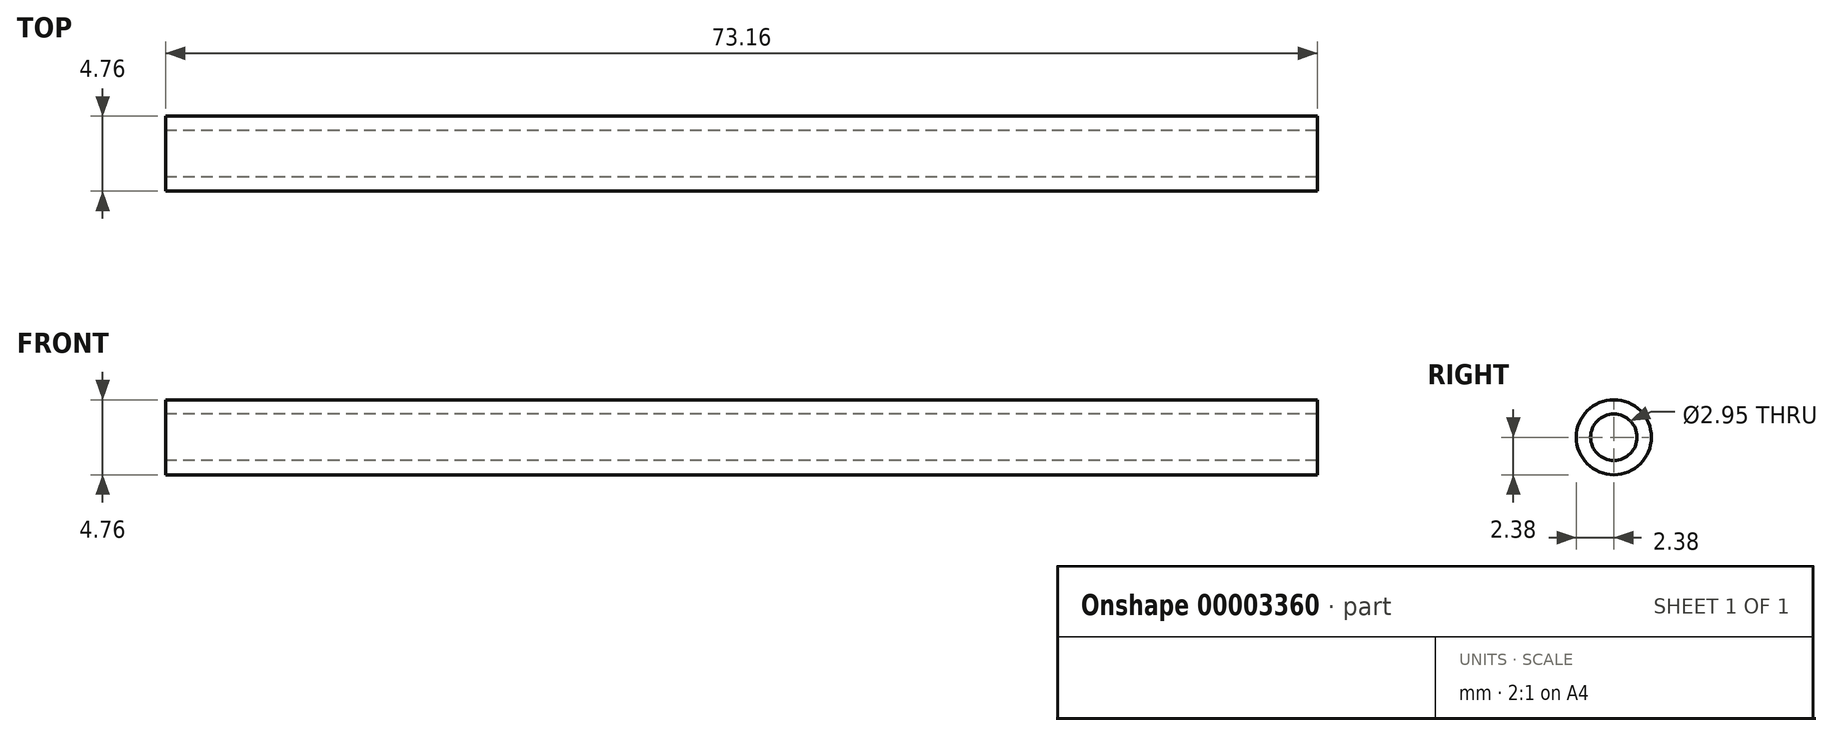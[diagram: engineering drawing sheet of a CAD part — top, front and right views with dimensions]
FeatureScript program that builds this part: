
annotation { "Feature Type Name" : "Feature", "Feature Type Description" : "" }
export const myFeature = defineFeature(function(context is Context, id is Id, definition is map)
    precondition{}
    {
        {
            var Q0;
            Q0=qCreatedBy(makeId("Right.planeOp"),FACE);
            var sketch = newSketch(context, id + "F0", { "sketchPlane" : qUnion([Q0])});
            skCircle(sketch, "E0", {"center": v(0, 0) * mm, "radius": 2.38 * mm});
            skCircle(sketch, "E1", {"center": v(0, 0) * mm, "radius": 1.47 * mm});
            skSolve(sketch);
        }
        {
            var Q0;
            Q0 = qSketchRegion(id + "F0", true);
            extrude(context, id + "F1", {"entities" : qUnion([Q0]), "endBound" : BoundingType.SYMMETRIC, "depth" : 73.15 * mm});
        }
    });
